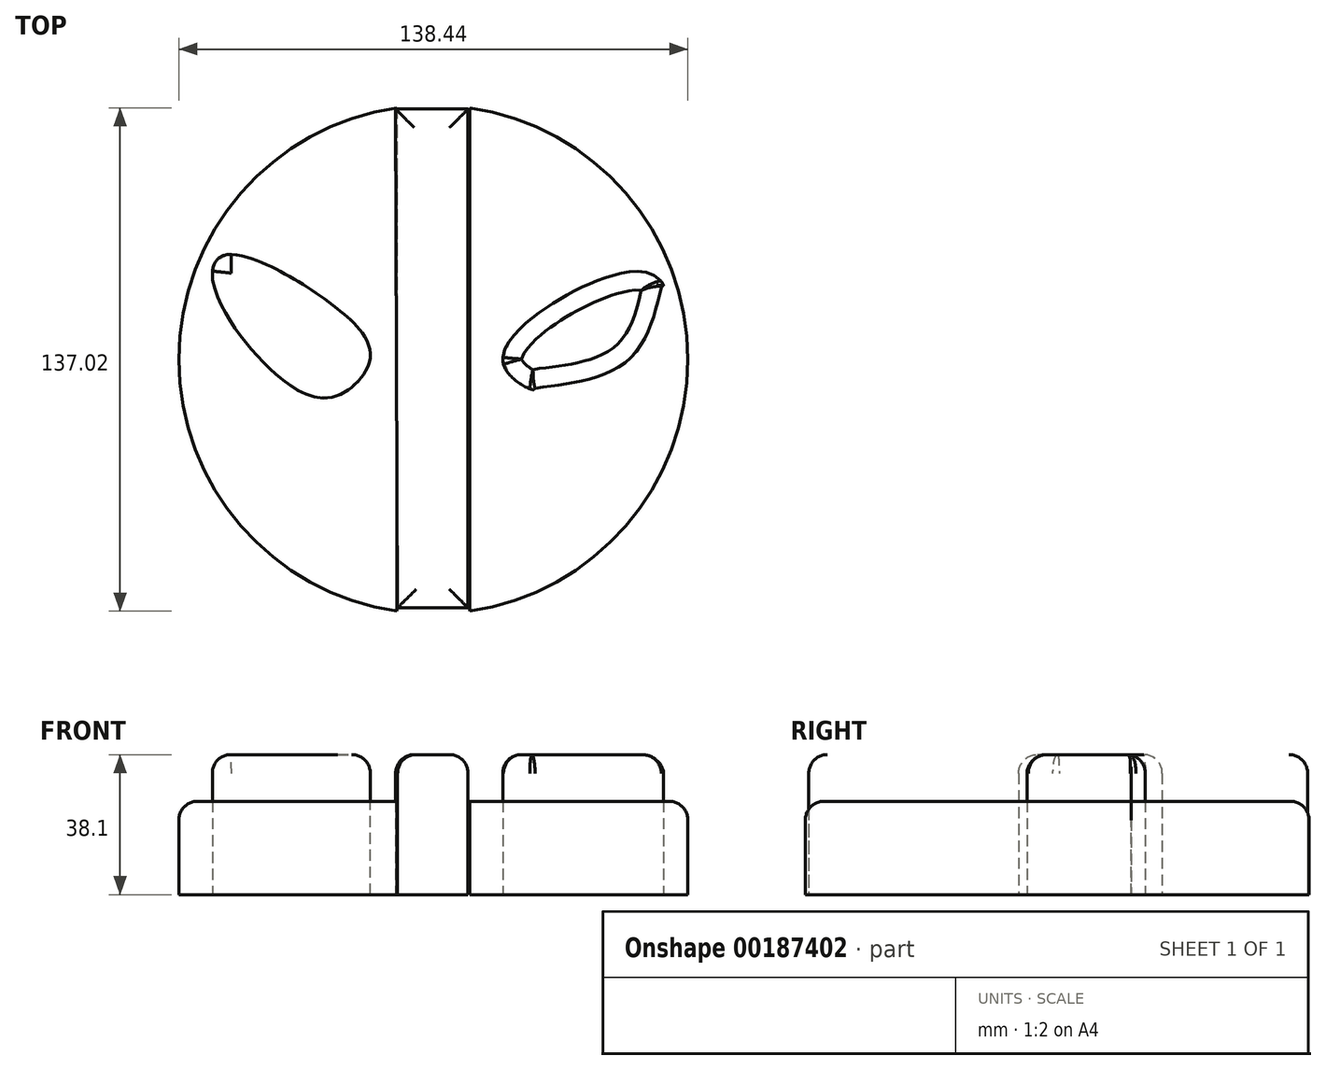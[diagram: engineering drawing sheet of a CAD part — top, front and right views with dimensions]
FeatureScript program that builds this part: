
annotation { "Feature Type Name" : "Feature", "Feature Type Description" : "" }
export const myFeature = defineFeature(function(context is Context, id is Id, definition is map)
    precondition{}
    {
        {
            var Q0;
            Q0=qCreatedBy(makeId("Top.planeOp"),FACE);
            var sketch = newSketch(context, id + "F0", { "sketchPlane" : qUnion([Q0])});
            skArc(sketch, "E0", {"start": v(9.87, -68.51) * mm, "mid": v(69.22, 0) * mm, "end": v(9.87, 68.51) * mm});
            skLineSegment(sketch, "E1", {"start": v(-9.87, 68.51) * mm, "end": v(-9.87, -68.51) * mm});
            skLineSegment(sketch, "E2", {"start": v(9.87, -70.57) * mm, "end": v(9.87, 68.51) * mm});
            skArc(sketch, "E3.trimOffspring", {"start": v(-9.87, 68.51) * mm, "mid": v(-69.22, 0) * mm, "end": v(-9.87, -68.51) * mm});
            skSolve(sketch);
        }
        {
            var Q0;
            Q0=makeQuery(id+"F0.imprint","IMPRINT",FACE,{"disambiguationData":[TD([[makeQuery(id+"F0.imprint","IMPRINT",EDGE,{"derivedFrom":sQuery(id+"F0.wireOp",EDGE,"E1")}),-1.0]])]});
            var sketch = newSketch(context, id + "F1", { "sketchPlane" : qUnion([Q0])});
            skLineSegment(sketch, "E4", {"start": v(-10.25, 68.14) * mm, "end": v(9.44, 68.14) * mm});
            skLineSegment(sketch, "E5", {"start": v(9.44, 69.76) * mm, "end": v(9.44, -67.6) * mm});
            skLineSegment(sketch, "E6", {"start": v(9.44, -67.6) * mm, "end": v(-9.71, -67.6) * mm});
            skLineSegment(sketch, "E7", {"start": v(-10.25, 68.14) * mm, "end": v(-9.71, -67.6) * mm});
            skFitSpline(sketch, "E8", {"points": [v(-26.18, 13.9) * mm, v(-17.27, 0) * mm, v(-26.98, -10.12) * mm, v(-42.9, -3.91) * mm, v(-59.9, 20.91) * mm, v(-56.4, 28.47) * mm, v(-26.18, 13.9) * mm]});
            skPoint(sketch, "E9.0.internal.orphan", {"position": v(24.97, 0) * mm});
            skFitSpline(sketch, "E10", {"points": [v(18.89, 0) * mm, v(27.25, -8.23) * mm, v(27.52, -7.96) * mm, v(53.16, 0) * mm, v(62.33, 20.1) * mm, v(62.6, 20.1) * mm, v(56.94, 23.88) * mm, v(18.89, 0) * mm]});
            skSolve(sketch);
        }
        {
            var Q0;
            Q0=sQuery(id+"F1.wireOp",EDGE,"E8");
            var Q1;
            Q1=sQuery(id+"F1.wireOp",EDGE,"E10");
            extrude(context, id + "F2", {"bodyType" : ToolBodyType.SURFACE, "surfaceEntities" : qUnion([Q0, Q1]), "depth" : 25.4 * mm});
        }
        {
            var Q0;
            Q0 = qSketchRegion(id + "F0", true);
            extrude(context, id + "F3", {"entities" : qUnion([Q0]), "depth" : 25.4 * mm});
        }
        {
            var Q0;
            Q0 = qSketchRegion(id + "F1", true);
            extrude(context, id + "F4", {"entities" : qUnion([Q0]), "depth" : 38.1 * mm});
        }
        {
            var Q0;
            Q0=makeQuery(id+"F3.opExtrude","CAP_EDGE",EDGE,{"disambiguationData":[OSD([sQuery(id+"F0.wireOp",EDGE,"E3.trimOffspring")])],"isStart":false});
            var Q1;
            Q1=makeQuery(id+"F3.opExtrude","CAP_EDGE",EDGE,{"disambiguationData":[OSD([sQuery(id+"F0.wireOp",EDGE,"E0")])],"isStart":false});
            var Q2;
            Q2=makeQuery(id+"F4.opExtrude","CAP_EDGE",EDGE,{"disambiguationData":[OSD([sQuery(id+"F1.wireOp",EDGE,"E4")])],"isStart":false});
            var Q3;
            Q3=makeQuery(id+"F4.opExtrude","CAP_EDGE",EDGE,{"disambiguationData":[OSD([sQuery(id+"F1.wireOp",EDGE,"E6")])],"isStart":false});
            var Q4;
            Q4=makeQuery(id+"F4.opExtrude","CAP_EDGE",EDGE,{"disambiguationData":[OSD([sQuery(id+"F1.wireOp",EDGE,"E7")])],"isStart":false});
            var Q5;
            Q5=makeQuery(id+"F4.opExtrude","CAP_EDGE",EDGE,{"disambiguationData":[OSD([sQuery(id+"F1.wireOp",EDGE,"E5")])],"isStart":false});
            var Q6;
            Q6=makeQuery(id+"F4.opExtrude","CAP_EDGE",EDGE,{"disambiguationData":[OSD([sQuery(id+"F1.wireOp",EDGE,"E8")])],"isStart":false});
            var Q7;
            Q7=makeQuery(id+"F4.opExtrude","CAP_EDGE",EDGE,{"disambiguationData":[OSD([sQuery(id+"F1.wireOp",EDGE,"E10")])],"isStart":false});
            fillet(context, id + "F5", {"entities" : qUnion([Q0, Q1, Q2, Q3, Q4, Q5, Q6, Q7]), "radius" : 5.08 * mm, "tangentPropagation" : true, "allowEdgeOverflow" : false});
        }
    });
